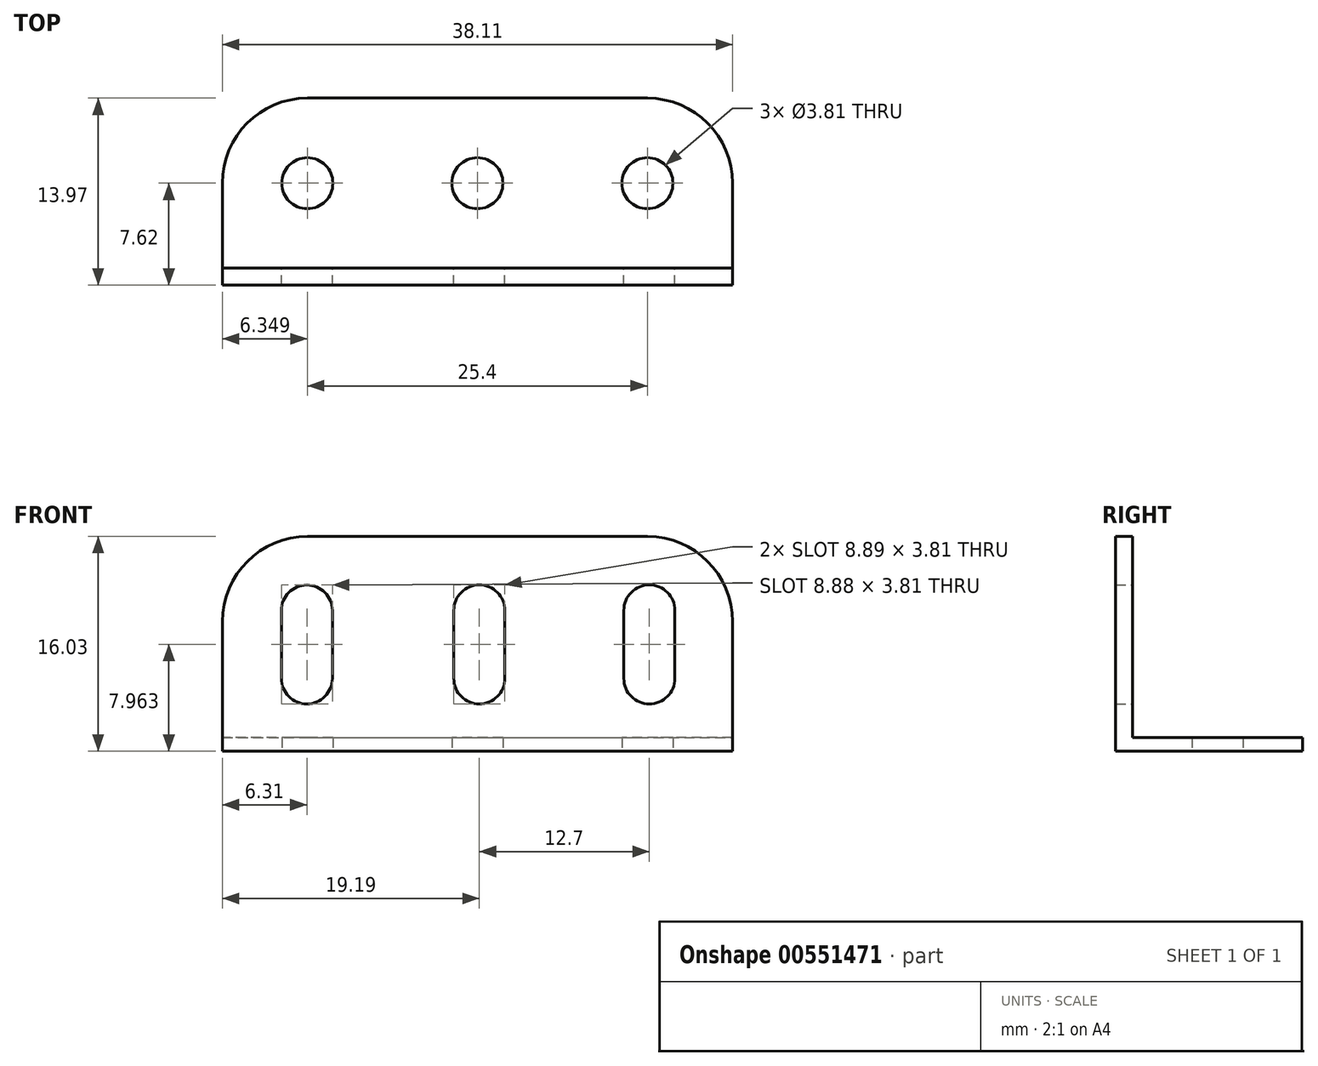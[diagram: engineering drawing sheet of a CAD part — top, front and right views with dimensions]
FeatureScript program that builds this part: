
annotation { "Feature Type Name" : "Feature", "Feature Type Description" : "" }
export const myFeature = defineFeature(function(context is Context, id is Id, definition is map)
    precondition{}
    {
        {
            var Q0;
            Q0=qCreatedBy(makeId("Top.planeOp"),FACE);
            var sketch = newSketch(context, id + "F0", { "sketchPlane" : qUnion([Q0])});
            skLineSegment(sketch, "E0.bottom", {"start": v(-15.54, 0) * mm, "end": v(22.56, 0) * mm});
            skLineSegment(sketch, "E0.top", {"start": v(-9.2, 12.7) * mm, "end": v(16.2, 12.7) * mm});
            skLineSegment(sketch, "E0.left", {"start": v(-15.54, 0) * mm, "end": v(-15.54, 6.35) * mm});
            skLineSegment(sketch, "E0.right", {"start": v(22.56, 0) * mm, "end": v(22.56, 6.35) * mm});
            skPoint(sketch, "E1.visualSharp", {"position": v(-15.54, 12.7) * mm});
            skArc(sketch, "E1.filletArc", {"start": v(-9.2, 12.7) * mm, "mid": v(-13.68, 10.84) * mm, "end": v(-15.54, 6.35) * mm});
            skPoint(sketch, "E2.visualSharp", {"position": v(22.56, 12.7) * mm});
            skArc(sketch, "E2.filletArc", {"start": v(22.56, 6.35) * mm, "mid": v(20.7, 10.84) * mm, "end": v(16.2, 12.7) * mm});
            skCircle(sketch, "E3", {"center": v(3.5, 6.35) * mm, "radius": 1.9 * mm});
            skCircle(sketch, "E4", {"center": v(-9.2, 6.35) * mm, "radius": 1.9 * mm});
            skCircle(sketch, "E5", {"center": v(16.2, 6.35) * mm, "radius": 1.9 * mm});
            skSolve(sketch);
        }
        {
            var Q0;
            Q0 = qSketchRegion(id + "F0", true);
            extrude(context, id + "F1", {"entities" : qUnion([Q0]), "depth" : 1.02 * mm, "offsetDistance" : 25.4 * mm});
        }
        {
            var Q0;
            Q0=qCreatedBy(makeId("Front.planeOp"),FACE);
            var sketch = newSketch(context, id + "F2", { "sketchPlane" : qUnion([Q0])});
            skLineSegment(sketch, "E6.bottom", {"start": v(-15.53, 0) * mm, "end": v(22.57, 0) * mm});
            skLineSegment(sketch, "E6.top", {"start": v(-9.18, 16.03) * mm, "end": v(16.22, 16.03) * mm});
            skLineSegment(sketch, "E6.left", {"start": v(-15.53, 0) * mm, "end": v(-15.53, 9.68) * mm});
            skLineSegment(sketch, "E6.right", {"start": v(22.57, 0) * mm, "end": v(22.57, 9.68) * mm});
            skPoint(sketch, "E7.middle", {"position": v(3.65, 7.96) * mm});
            skPoint(sketch, "E8.middle", {"position": v(17.45, 7.96) * mm});
            skPoint(sketch, "E9.visualSharp", {"position": v(-15.53, 16.03) * mm});
            skArc(sketch, "E9.filletArc", {"start": v(-9.18, 16.03) * mm, "mid": v(-13.67, 14.17) * mm, "end": v(-15.53, 9.68) * mm});
            skPoint(sketch, "E10.visualSharp", {"position": v(22.57, 16.03) * mm});
            skArc(sketch, "E10.filletArc", {"start": v(22.57, 9.68) * mm, "mid": v(20.7, 14.17) * mm, "end": v(16.22, 16.03) * mm});
            skLineSegment(sketch, "E11.bottom", {"start": v(5.56, 5.42) * mm, "end": v(1.75, 5.42) * mm});
            skLineSegment(sketch, "E11.top", {"start": v(5.56, 10.5) * mm, "end": v(1.75, 10.5) * mm});
            skLineSegment(sketch, "E11.left", {"start": v(5.56, 5.42) * mm, "end": v(5.56, 10.5) * mm});
            skLineSegment(sketch, "E11.right", {"start": v(1.75, 5.42) * mm, "end": v(1.75, 10.5) * mm});
            skLineSegment(sketch, "E12.bottom", {"start": v(14.45, 5.42) * mm, "end": v(18.26, 5.42) * mm});
            skLineSegment(sketch, "E12.top", {"start": v(14.45, 10.5) * mm, "end": v(18.26, 10.5) * mm});
            skLineSegment(sketch, "E12.left", {"start": v(14.45, 5.42) * mm, "end": v(14.45, 10.5) * mm});
            skLineSegment(sketch, "E12.right", {"start": v(18.26, 5.42) * mm, "end": v(18.26, 10.5) * mm});
            skPoint(sketch, "E12.middle", {"position": v(16.35, 7.96) * mm});
            skArc(sketch, "E13", {"start": v(5.56, 10.5) * mm, "mid": v(3.65, 12.4) * mm, "end": v(1.75, 10.5) * mm});
            skArc(sketch, "E14", {"start": v(5.56, 5.42) * mm, "mid": v(3.65, 3.52) * mm, "end": v(1.75, 5.42) * mm});
            skArc(sketch, "E15", {"start": v(18.26, 10.5) * mm, "mid": v(16.35, 12.4) * mm, "end": v(14.45, 10.5) * mm});
            skArc(sketch, "E16", {"start": v(18.26, 5.42) * mm, "mid": v(16.35, 3.52) * mm, "end": v(14.45, 5.42) * mm});
            skPoint(sketch, "E17.middle.positionSnap0", {"position": v(1.75, 7.96) * mm});
            skPoint(sketch, "E17.centerSnap0", {"position": v(1.75, 7.96) * mm});
            skLineSegment(sketch, "E18", {"start": v(3.65, 20.7) * mm, "end": v(-9.05, 20.7) * mm});
            skLineSegment(sketch, "E19.bottom", {"start": v(-11.14, 5.43) * mm, "end": v(-7.33, 5.43) * mm});
            skLineSegment(sketch, "E19.top", {"start": v(-11.14, 10.5) * mm, "end": v(-7.33, 10.5) * mm});
            skLineSegment(sketch, "E19.left", {"start": v(-11.14, 5.43) * mm, "end": v(-11.14, 10.5) * mm});
            skLineSegment(sketch, "E19.right", {"start": v(-7.33, 5.43) * mm, "end": v(-7.33, 10.5) * mm});
            skPoint(sketch, "E19.middle", {"position": v(-9.23, 7.96) * mm});
            skArc(sketch, "E20", {"start": v(-7.33, 10.5) * mm, "mid": v(-9.23, 12.4) * mm, "end": v(-11.14, 10.5) * mm});
            skArc(sketch, "E21", {"start": v(-7.33, 5.43) * mm, "mid": v(-9.23, 3.53) * mm, "end": v(-11.14, 5.43) * mm});
            skSolve(sketch);
        }
        {
            var Q0;
            Q0 = qSketchRegion(id + "F2", true);
            extrude(context, id + "F3", {"entities" : qUnion([Q0]), "operationType" : NewBodyOperationType.ADD, "depth" : 1.27 * mm, "offsetDistance" : 25.4 * mm});
        }
    });
